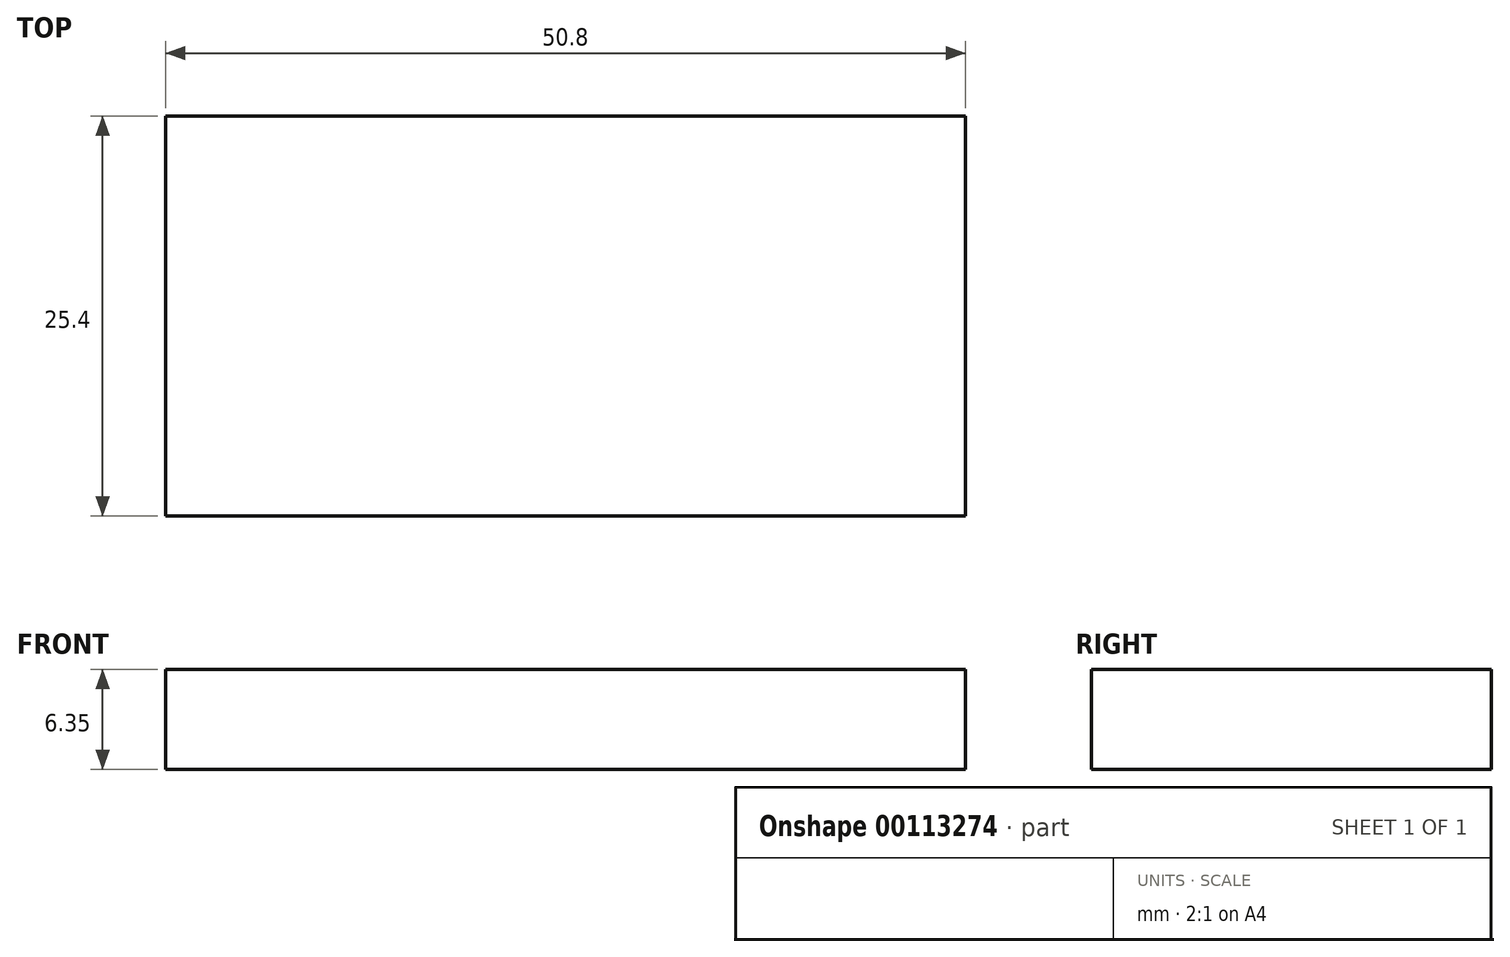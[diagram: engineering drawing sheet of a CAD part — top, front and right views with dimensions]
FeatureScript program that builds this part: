
annotation { "Feature Type Name" : "Feature", "Feature Type Description" : "" }
export const myFeature = defineFeature(function(context is Context, id is Id, definition is map)
    precondition{}
    {
        {
            var Q0;
            Q0=qCreatedBy(makeId("Top.planeOp"),FACE);
            var sketch = newSketch(context, id + "F0", { "sketchPlane" : qUnion([Q0])});
            skLineSegment(sketch, "E0.bottom", {"start": v(25.4, -12.7) * mm, "end": v(-25.4, -12.7) * mm});
            skLineSegment(sketch, "E0.top", {"start": v(25.4, 12.7) * mm, "end": v(-25.4, 12.7) * mm});
            skLineSegment(sketch, "E0.left", {"start": v(25.4, -12.7) * mm, "end": v(25.4, 12.7) * mm});
            skLineSegment(sketch, "E0.right", {"start": v(-25.4, -12.7) * mm, "end": v(-25.4, 12.7) * mm});
            skPoint(sketch, "E0.middle", {"position": v(0, 0) * mm});
            skSolve(sketch);
        }
        {
            var Q0;
            Q0 = qSketchRegion(id + "F0", true);
            extrude(context, id + "F1", {"entities" : qUnion([Q0]), "depth" : 6.35 * mm});
        }
    });
